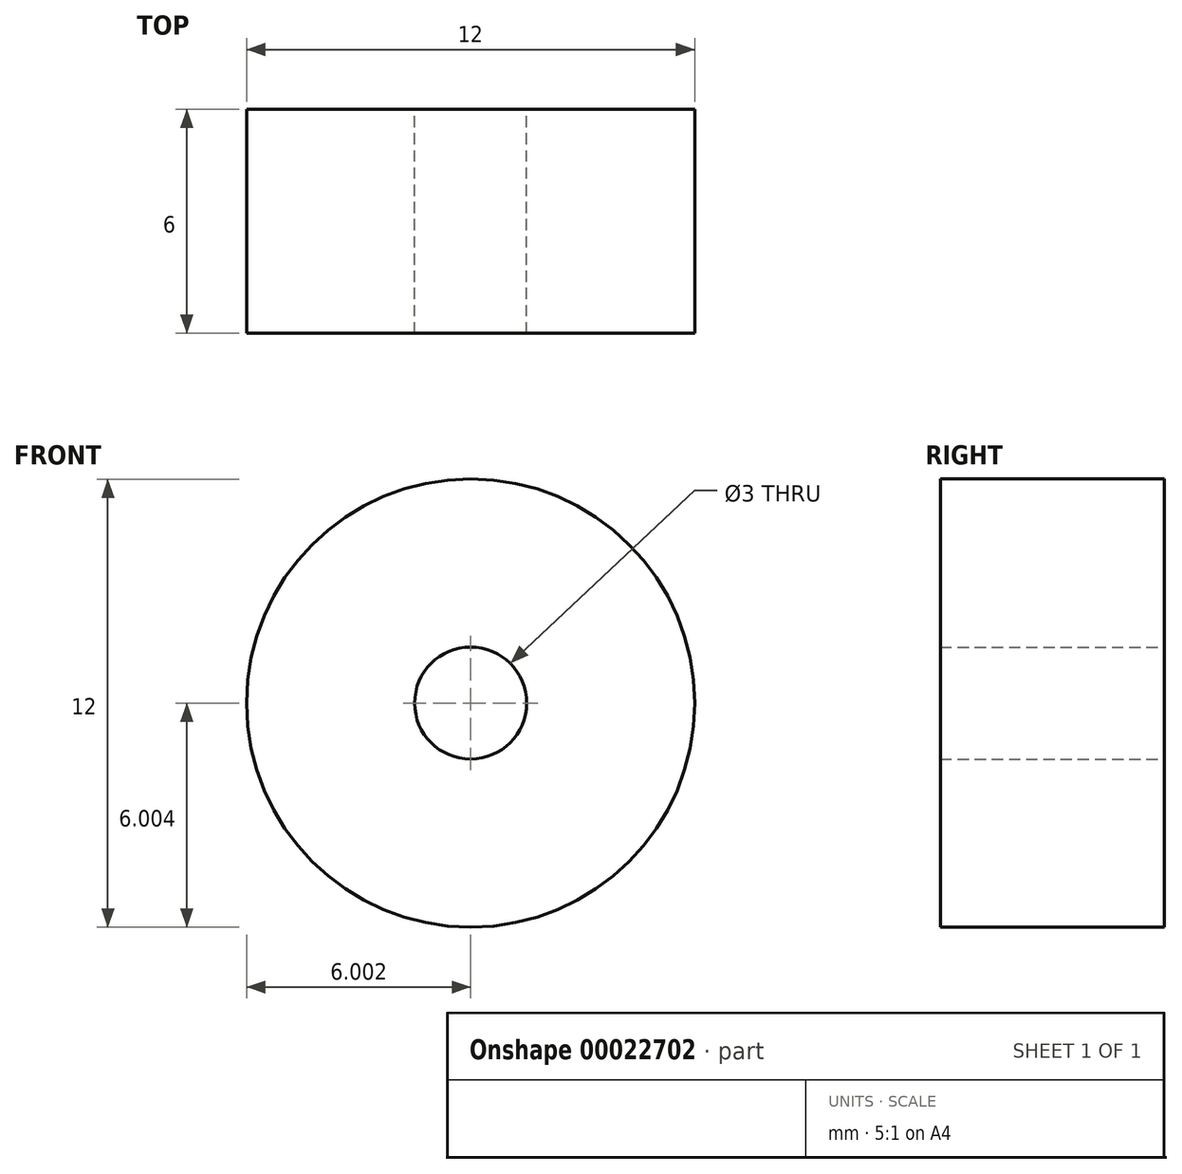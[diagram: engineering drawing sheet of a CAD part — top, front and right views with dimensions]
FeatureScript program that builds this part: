
annotation { "Feature Type Name" : "Feature", "Feature Type Description" : "" }
export const myFeature = defineFeature(function(context is Context, id is Id, definition is map)
    precondition{}
    {
        {
            var Q0;
            Q0=qCreatedBy(makeId("Front.planeOp"),FACE);
            var sketch = newSketch(context, id + "F0", { "sketchPlane" : qUnion([Q0])});
            skCircle(sketch, "E0", {"center": v(-45.26, 29.02) * mm, "radius": 6 * mm});
            skCircle(sketch, "E1", {"center": v(-45.26, 29.02) * mm, "radius": 1.5 * mm});
            skSolve(sketch);
        }
        {
            var Q0;
            Q0=makeQuery(id+"F0.imprint","IMPRINT",FACE,{"disambiguationData":[TD([[makeQuery(id+"F0.imprint","IMPRINT",EDGE,{"derivedFrom":sQuery(id+"F0.wireOp",EDGE,"E0")}),1.0]])]});
            extrude(context, id + "F1", {"entities" : qUnion([Q0]), "endBound" : BoundingType.SYMMETRIC, "depth" : 6 * mm});
        }
    });
